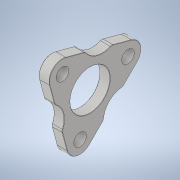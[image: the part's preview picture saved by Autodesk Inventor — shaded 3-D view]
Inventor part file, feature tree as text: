
AUTODESK INVENTOR PART (.ipt)
format: ipt  version: 2021 (Build 250183000, 183)  size: 206,848 bytes
history: native  units: in
note: dims shown in document units (in); Inventor stores cm internally (conversion verified against a paired STEP export)
features: extrude x2, chamfer x2, sketch x2, fillet x1
ambient origin geometry x8: Origin, YZ Plane, XZ Plane, XY Plane, X Axis, Y Axis, Z Axis, Center Point
bodies: Solid1 (feature_tree)
feature tree (7):
  extrude  "Extrusion1"  Depth=0.325in TaperAngle=0.0deg
  extrude  "Extrusion2"  Depth=0.125in
  fillet  "Fillet1"  Radius=1.05in
  chamfer  "Chamfer1"  Distance=1.1811in Angle=360.0deg
  chamfer  "Chamfer2"  Distance=0.325in
  sketch  "Sketch1"  dims[d0=0.825in d1=0.825in d2=0.825in d3=1.25in d4=0.325in d5=0.0in]
  sketch  "Sketch2"  dims[d6=45.0deg d7=1.25in d8=1.05in d9=1.1811in d11=360.0deg d13=0.325in d14=0.0in d15=0.125in d16=0.01in d17=0.125in d18=45.0deg d19=0.01in d20=0.125in d21=45.0deg]
